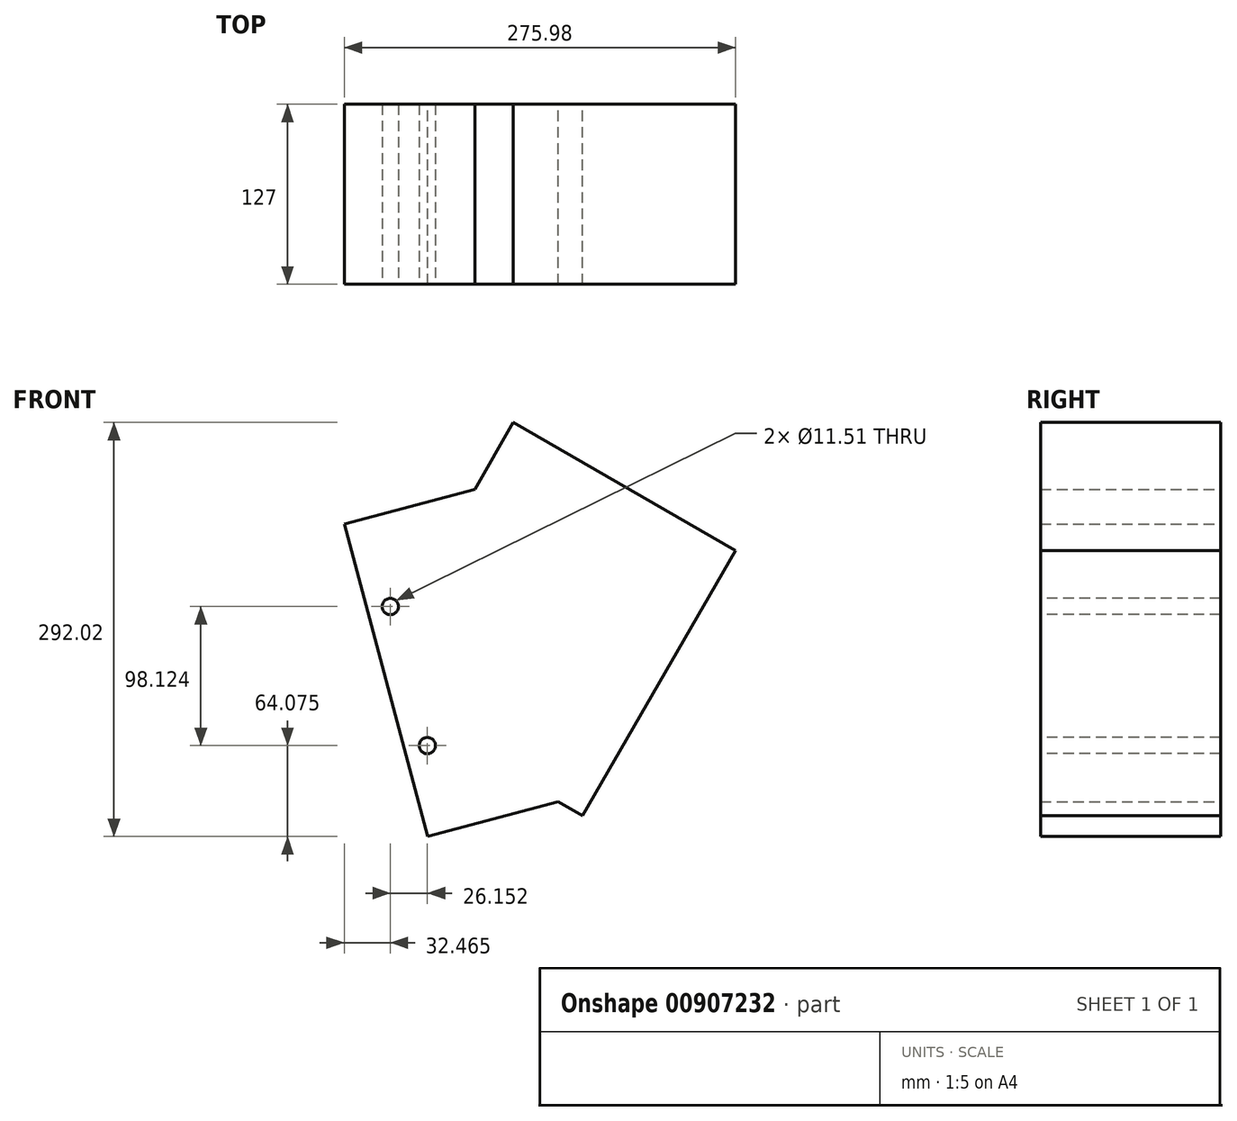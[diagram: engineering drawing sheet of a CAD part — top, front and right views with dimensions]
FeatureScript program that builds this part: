
annotation { "Feature Type Name" : "Feature", "Feature Type Description" : "" }
export const myFeature = defineFeature(function(context is Context, id is Id, definition is map)
    precondition{}
    {
        {
            var Q0;
            Q0=qCreatedBy(makeId("Front.planeOp"),FACE);
            var sketch = newSketch(context, id + "F0", { "sketchPlane" : qUnion([Q0])});
            skLineSegment(sketch, "E0", {"start": v(0, 0) * mm, "end": v(107.95, 186.97) * mm});
            skLineSegment(sketch, "E1", {"start": v(107.95, 186.97) * mm, "end": v(-48.78, 277.46) * mm});
            skLineSegment(sketch, "E2", {"start": v(-48.78, 277.46) * mm, "end": v(-76, 230.32) * mm});
            skLineSegment(sketch, "E3", {"start": v(-76, 230.32) * mm, "end": v(-17.27, 9.97) * mm});
            skLineSegment(sketch, "E4", {"start": v(-17.27, 9.97) * mm, "end": v(0, 0) * mm});
            skLineSegment(sketch, "E5", {"start": v(-76, 230.32) * mm, "end": v(-168.03, 205.8) * mm});
            skLineSegment(sketch, "E6", {"start": v(-168.03, 205.8) * mm, "end": v(-109.3, -14.56) * mm});
            skLineSegment(sketch, "E7", {"start": v(-109.3, -14.56) * mm, "end": v(-17.27, 9.97) * mm});
            skSolve(sketch);
        }
        {
            var Q0;
            Q0 = qSketchRegion(id + "F0", true);
            extrude(context, id + "F1", {"entities" : qUnion([Q0]), "depth" : 127 * mm, "offsetDistance" : 25.4 * mm});
        }
        {
            var Q0;
            Q0=makeQuery(id+"F1.opExtrude","CAP_FACE",FACE,{"disambiguationData":[OSD([sQuery(id+"F0.wireOp",EDGE,"E0"),sQuery(id+"F0.wireOp",EDGE,"E1"),sQuery(id+"F0.wireOp",EDGE,"E2"),sQuery(id+"F0.wireOp",EDGE,"E4"),sQuery(id+"F0.wireOp",EDGE,"E5"),sQuery(id+"F0.wireOp",EDGE,"E6"),sQuery(id+"F0.wireOp",EDGE,"E7")])],"isStart":true});
            var sketch = newSketch(context, id + "F2", { "sketchPlane" : qUnion([Q0])});
            skPoint(sketch, "E8", {"position": v(135.57, 147.64) * mm});
            skPoint(sketch, "E9", {"position": v(109.41, 49.51) * mm});
            skCircle(sketch, "E10", {"center": v(135.57, 147.64) * mm, "radius": 5.37 * mm, "construction": true});
            skCircle(sketch, "E11", {"center": v(109.41, 49.51) * mm, "radius": 5.37 * mm, "construction": true});
            skSolve(sketch);
        }
        {
            var Q0;
            Q0=sQuery(id+"F2.wireOp",VERTEX,"E8");
            var Q1;
            Q1=sQuery(id+"F2.wireOp",VERTEX,"E9");
            var Q2;
            Q2=makeQuery(id+"F1.opExtrude","SWEPT_BODY",BODY,{"disambiguationData":[OSD([sQuery(id+"F0.wireOp",EDGE,"E0"),sQuery(id+"F0.wireOp",EDGE,"E1"),sQuery(id+"F0.wireOp",EDGE,"E2"),sQuery(id+"F0.wireOp",EDGE,"E4"),sQuery(id+"F0.wireOp",EDGE,"E5"),sQuery(id+"F0.wireOp",EDGE,"E6"),sQuery(id+"F0.wireOp",EDGE,"E7")])]});
            hole(context, id + "F3", {"style" : HoleStyle.SIMPLE, "endStyle" : HoleEndStyle.THROUGH, "standardTappedOrClearance" : lookupTablePath({ "standard" : "ANSI", "engagement" : "75%", "pitch" : "20 tpi", "size" : "1/2", "type" : "Tapped" }), "standardBlindInLast" : lookupTablePath({ "standard" : "ANSI", "fit" : "Free", "engagement" : "75%", "pitch" : "20 tpi", "size" : "1/2", "type" : "Clearance & tapped" }), "holeDiameter" : 11.5 * mm, "majorDiameter" : 12.7 * mm, "showTappedDepth" : true, "isTappedThrough" : true, "tappedDepth" : 8.47 * mm, "tapClearance" : 3, "locations" : qUnion([Q0, Q1]), "scope" : qUnion([Q2]), "startStyle" : HoleStartStyle.SKETCH});
        }
    });
